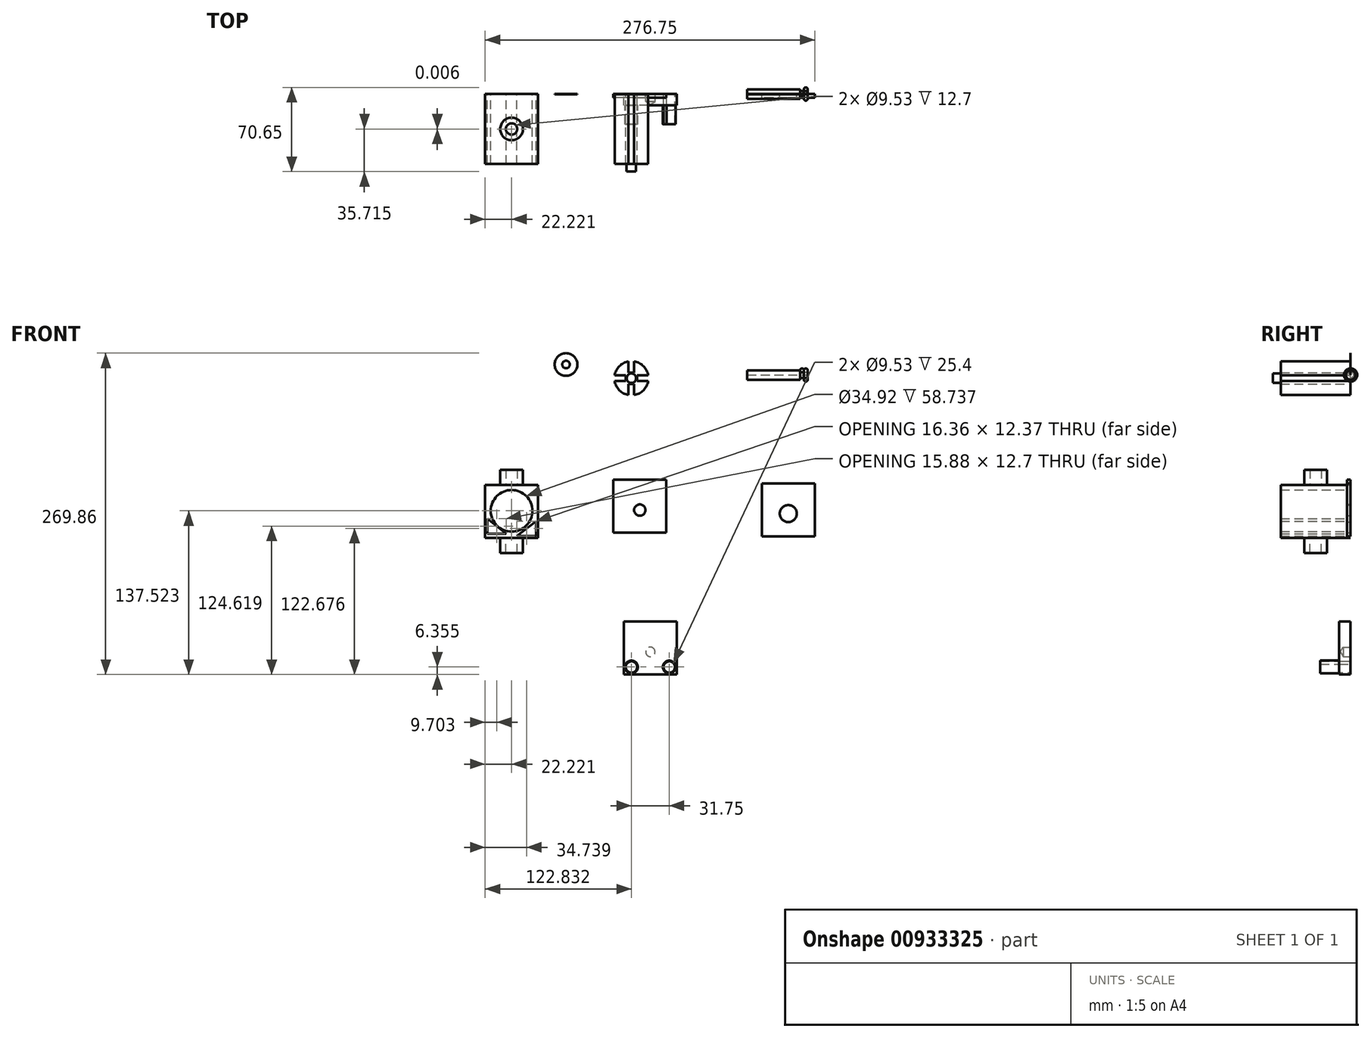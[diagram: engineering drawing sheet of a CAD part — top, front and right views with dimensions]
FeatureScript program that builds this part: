
annotation { "Feature Type Name" : "Feature", "Feature Type Description" : "" }
export const myFeature = defineFeature(function(context is Context, id is Id, definition is map)
    precondition{}
    {
        {
            var Q0;
            Q0=qCreatedBy(makeId("Front.planeOp"),FACE);
            var sketch = newSketch(context, id + "F0", { "sketchPlane" : qUnion([Q0])});
            skLineSegment(sketch, "E0.bottom", {"start": v(22.22, -22.22) * mm, "end": v(-22.23, -22.23) * mm});
            skLineSegment(sketch, "E0.top", {"start": v(22.22, 22.23) * mm, "end": v(-22.23, 22.22) * mm});
            skLineSegment(sketch, "E0.left", {"start": v(22.22, -22.22) * mm, "end": v(22.22, 22.23) * mm});
            skLineSegment(sketch, "E0.right", {"start": v(-22.23, -22.23) * mm, "end": v(-22.23, 22.23) * mm});
            skPoint(sketch, "E0.middle", {"position": v(0, 0) * mm});
            skCircle(sketch, "E1", {"center": v(0, 0) * mm, "radius": 17.46 * mm});
            skCircle(sketch, "E2", {"center": v(0, -3.18) * mm, "radius": 14.29 * mm, "construction": true});
            skCircle(sketch, "E3", {"center": v(0, -3.18) * mm, "radius": 7.14 * mm});
            skCircle(sketch, "E4", {"center": v(0, -3.18) * mm, "radius": 4.76 * mm});
            skLineSegment(sketch, "E5.bottom", {"start": v(-85.38, -26.4) * mm, "end": v(-129.83, -26.4) * mm});
            skLineSegment(sketch, "E5.top", {"start": v(-85.38, 18.05) * mm, "end": v(-129.83, 18.05) * mm});
            skLineSegment(sketch, "E5.left", {"start": v(-85.38, -26.4) * mm, "end": v(-85.38, 18.05) * mm});
            skLineSegment(sketch, "E5.right", {"start": v(-129.83, -26.4) * mm, "end": v(-129.83, 18.05) * mm});
            skCircle(sketch, "E6", {"center": v(-107.6, -3.79) * mm, "radius": 17.46 * mm});
            skCircle(sketch, "E7", {"center": v(-107.6, -6.96) * mm, "radius": 14.29 * mm, "construction": true});
            skCircle(sketch, "E8", {"center": v(-107.6, -6.96) * mm, "radius": 7.14 * mm});
            skCircle(sketch, "E9", {"center": v(-107.6, -6.96) * mm, "radius": 4.76 * mm});
            skLineSegment(sketch, "E10.bottom", {"start": v(146.92, -25.18) * mm, "end": v(102.47, -25.18) * mm});
            skLineSegment(sketch, "E10.top", {"start": v(146.92, 19.27) * mm, "end": v(102.47, 19.27) * mm});
            skLineSegment(sketch, "E10.left", {"start": v(146.92, -25.18) * mm, "end": v(146.92, 19.27) * mm});
            skLineSegment(sketch, "E10.right", {"start": v(102.47, -25.18) * mm, "end": v(102.47, 19.27) * mm});
            skCircle(sketch, "E11", {"center": v(124.7, -2.96) * mm, "radius": 17.46 * mm});
            skCircle(sketch, "E12", {"center": v(124.7, -6.13) * mm, "radius": 14.29 * mm, "construction": true});
            skCircle(sketch, "E13", {"center": v(124.7, -6.13) * mm, "radius": 7.14 * mm});
            skCircle(sketch, "E14", {"center": v(124.7, -6.13) * mm, "radius": 4.76 * mm});
            skLineSegment(sketch, "E15.bottom", {"start": v(31.1, -141.3) * mm, "end": v(-13.35, -141.3) * mm});
            skLineSegment(sketch, "E15.top", {"start": v(31.1, -96.86) * mm, "end": v(-13.35, -96.86) * mm});
            skLineSegment(sketch, "E15.left", {"start": v(31.1, -141.3) * mm, "end": v(31.1, -96.86) * mm});
            skLineSegment(sketch, "E15.right", {"start": v(-13.35, -141.3) * mm, "end": v(-13.35, -96.86) * mm});
            skCircle(sketch, "E16", {"center": v(8.88, -119.08) * mm, "radius": 17.46 * mm});
            skCircle(sketch, "E17", {"center": v(8.88, -122.26) * mm, "radius": 14.29 * mm, "construction": true});
            skCircle(sketch, "E18", {"center": v(8.88, -122.26) * mm, "radius": 7.14 * mm});
            skCircle(sketch, "E19", {"center": v(8.88, -122.26) * mm, "radius": 4.76 * mm});
            skCircle(sketch, "E20", {"center": v(8.88, -122.26) * mm, "radius": 3.97 * mm});
            skLineSegment(sketch, "E21", {"start": v(-86.91, -24.82) * mm, "end": v(-103.27, -24.82) * mm});
            skLineSegment(sketch, "E22", {"start": v(-103.27, -24.82) * mm, "end": v(-87.15, -12.45) * mm});
            skLineSegment(sketch, "E23", {"start": v(-87.15, -12.45) * mm, "end": v(-86.91, -24.82) * mm});
            skLineSegment(sketch, "E24", {"start": v(-112.19, -23.04) * mm, "end": v(-128.06, -23.04) * mm});
            skLineSegment(sketch, "E25", {"start": v(-128.06, -23.04) * mm, "end": v(-128.06, -10.34) * mm});
            skLineSegment(sketch, "E26", {"start": v(-128.06, -10.34) * mm, "end": v(-112.19, -23.04) * mm});
            skCircle(sketch, "E27", {"center": v(24.75, -134.96) * mm, "radius": 5.4 * mm});
            skCircle(sketch, "E28", {"center": v(-7, -134.96) * mm, "radius": 5.4 * mm});
            skCircle(sketch, "E29", {"center": v(24.75, -134.96) * mm, "radius": 4.76 * mm});
            skCircle(sketch, "E30", {"center": v(-7, -134.96) * mm, "radius": 4.76 * mm});
            skSolve(sketch);
        }
        {
            var Q0;
            Q0=makeQuery(id+"F0.imprint","IMPRINT",FACE,{"disambiguationData":[TD([[makeQuery(id+"F0.imprint","IMPRINT",EDGE,{"derivedFrom":sQuery(id+"F0.wireOp",EDGE,"E3")}),1.0]])]});
            var Q1;
            Q1=makeQuery(id+"F0.imprint","IMPRINT",FACE,{"disambiguationData":[TD([[makeQuery(id+"F0.imprint","IMPRINT",EDGE,{"derivedFrom":sQuery(id+"F0.wireOp",EDGE,"E0.bottom")}),-1.0]])]});
            var Q2;
            Q2=makeQuery(id+"F0.imprint","IMPRINT",FACE,{"disambiguationData":[TD([[makeQuery(id+"F0.imprint","IMPRINT",EDGE,{"derivedFrom":sQuery(id+"F0.wireOp",EDGE,"E1")}),1.0]])]});
            extrude(context, id + "F1", {"entities" : qUnion([Q0, Q1, Q2]), "depth" : 3.17 * mm, "offsetDistance" : 25.4 * mm});
        }
        {
            var Q0;
            Q0=makeQuery(id+"F0.imprint","IMPRINT",FACE,{"disambiguationData":[TD([[makeQuery(id+"F0.imprint","IMPRINT",EDGE,{"derivedFrom":sQuery(id+"F0.wireOp",EDGE,"E11")}),1.0]])]});
            var Q1;
            Q1=makeQuery(id+"F0.imprint","IMPRINT",FACE,{"disambiguationData":[TD([[makeQuery(id+"F0.imprint","IMPRINT",EDGE,{"derivedFrom":sQuery(id+"F0.wireOp",EDGE,"E10.bottom")}),-1.0]])]});
            extrude(context, id + "F2", {"entities" : qUnion([Q0, Q1]), "depth" : 3.17 * mm, "offsetDistance" : 25.4 * mm});
        }
        {
            var Q0;
            Q0=makeQuery(id+"F0.imprint","IMPRINT",FACE,{"disambiguationData":[TD([[makeQuery(id+"F0.imprint","IMPRINT",EDGE,{"derivedFrom":sQuery(id+"F0.wireOp",EDGE,"E5.bottom")}),-1.0]])]});
            extrude(context, id + "F3", {"entities" : qUnion([Q0]), "depth" : 58.74 * mm, "offsetDistance" : 25.4 * mm});
        }
        {
            var Q0;
            Q0=makeQuery(id+"F0.imprint","IMPRINT",FACE,{"disambiguationData":[TD([[makeQuery(id+"F0.imprint","IMPRINT",EDGE,{"derivedFrom":sQuery(id+"F0.wireOp",EDGE,"E18")}),1.0]])]});
            var Q1;
            Q1=makeQuery(id+"F0.imprint","IMPRINT",FACE,{"disambiguationData":[TD([[makeQuery(id+"F0.imprint","IMPRINT",EDGE,{"derivedFrom":sQuery(id+"F0.wireOp",EDGE,"E19")}),1.0]])]});
            var Q2;
            Q2=makeQuery(id+"F0.imprint","IMPRINT",FACE,{"disambiguationData":[TD([[makeQuery(id+"F0.imprint","IMPRINT",EDGE,{"derivedFrom":sQuery(id+"F0.wireOp",EDGE,"E20")}),1.0]])]});
            var Q3;
            Q3=makeQuery(id+"F0.imprint","IMPRINT",FACE,{"disambiguationData":[TD([[makeQuery(id+"F0.imprint","IMPRINT",EDGE,{"derivedFrom":sQuery(id+"F0.wireOp",EDGE,"E16")}),1.0]])]});
            var Q4;
            Q4=makeQuery(id+"F0.imprint","IMPRINT",FACE,{"disambiguationData":[TD([[makeQuery(id+"F0.imprint","IMPRINT",EDGE,{"derivedFrom":sQuery(id+"F0.wireOp",EDGE,"E15.bottom")}),-1.0]])]});
            extrude(context, id + "F4", {"entities" : qUnion([Q0, Q1, Q2, Q3, Q4]), "depth" : 9.52 * mm, "offsetDistance" : 25.4 * mm});
        }
        {
            var Q0;
            Q0=sQuery(id+"F0.wireOp",VERTEX,"E19.center");
            var Q1;
            Q1=makeQuery(id+"F4.opExtrude","SWEPT_BODY",BODY,{"disambiguationData":[OSD([sQuery(id+"F0.wireOp",EDGE,"E15.bottom"),sQuery(id+"F0.wireOp",EDGE,"E15.top"),sQuery(id+"F0.wireOp",EDGE,"E15.left"),sQuery(id+"F0.wireOp",EDGE,"E15.right")])]});
            hole(context, id + "F5", {"style" : HoleStyle.SIMPLE, "endStyle" : HoleEndStyle.BLIND, "oppositeDirection" : true, "holeDiameter" : 7.94 * mm, "majorDiameter" : 6.35 * mm, "holeDepth" : 6.35 * mm, "isTappedThrough" : true, "tappedDepth" : 12.7 * mm, "tapClearance" : 3, "locations" : qUnion([Q0]), "scope" : qUnion([Q1])});
        }
        {
            var Q0;
            Q0=qCreatedBy(makeId("Front.planeOp"),FACE);
            var sketch = newSketch(context, id + "F6", { "sketchPlane" : qUnion([Q0])});
            skArc(sketch, "E31", {"start": v(-4.66, 93.43) * mm, "mid": v(3.06, 97.41) * mm, "end": v(7.05, 105.14) * mm});
            skCircle(sketch, "E32", {"center": v(-7.04, 107.52) * mm, "radius": 3.97 * mm});
            skLineSegment(sketch, "E33.left", {"start": v(-4.66, 93.43) * mm, "end": v(-4.66, 102.75) * mm});
            skLineSegment(sketch, "E33.right", {"start": v(-9.42, 93.43) * mm, "end": v(-9.42, 102.75) * mm});
            skLineSegment(sketch, "E34.bottom", {"start": v(7.05, 105.14) * mm, "end": v(-2.28, 105.14) * mm});
            skLineSegment(sketch, "E34.top", {"start": v(7.05, 109.9) * mm, "end": v(-2.28, 109.9) * mm});
            skLineSegment(sketch, "E35", {"start": v(-9.42, 112.28) * mm, "end": v(-4.66, 112.28) * mm});
            skLineSegment(sketch, "E36.bottom", {"start": v(-4.66, 102.75) * mm, "end": v(-9.42, 102.75) * mm});
            skLineSegment(sketch, "E36.top", {"start": v(-4.66, 112.28) * mm, "end": v(-9.42, 112.28) * mm});
            skLineSegment(sketch, "E36.left", {"start": v(-2.28, 105.14) * mm, "end": v(-2.28, 109.9) * mm});
            skLineSegment(sketch, "E36.right", {"start": v(-11.8, 105.14) * mm, "end": v(-11.8, 109.9) * mm});
            skArc(sketch, "E37.trimOffspring", {"start": v(7.05, 109.9) * mm, "mid": v(3.06, 117.62) * mm, "end": v(-4.66, 121.6) * mm});
            skLineSegment(sketch, "E38.trimOffspring", {"start": v(-4.66, 112.28) * mm, "end": v(-4.66, 121.6) * mm});
            skLineSegment(sketch, "E39.trimOffspring", {"start": v(-11.8, 105.14) * mm, "end": v(-21.13, 105.14) * mm});
            skLineSegment(sketch, "E40.trimOffspring", {"start": v(-9.42, 112.28) * mm, "end": v(-9.42, 121.6) * mm});
            skArc(sketch, "E41.trimOffspring", {"start": v(-9.42, 121.6) * mm, "mid": v(-17.14, 117.62) * mm, "end": v(-21.13, 109.9) * mm});
            skLineSegment(sketch, "E42.trimOffspring", {"start": v(-11.8, 109.9) * mm, "end": v(-21.13, 109.9) * mm});
            skArc(sketch, "E43.trimOffspring", {"start": v(-21.13, 105.14) * mm, "mid": v(-17.14, 97.41) * mm, "end": v(-9.42, 93.43) * mm});
            skLineSegment(sketch, "E44", {"start": v(90.13, 110.2) * mm, "end": v(140.93, 110.2) * mm});
            skLineSegment(sketch, "E45", {"start": v(140.93, 110.2) * mm, "end": v(140.93, 114.17) * mm});
            skLineSegment(sketch, "E46", {"start": v(90.13, 114.17) * mm, "end": v(90.13, 110.2) * mm});
            skCircle(sketch, "E47", {"center": v(139.34, 114.17) * mm, "radius": 1.59 * mm});
            skCircle(sketch, "E48", {"center": v(136.17, 114.17) * mm, "radius": 1.59 * mm});
            skLineSegment(sketch, "E49.trimOffspring", {"start": v(134.58, 114.17) * mm, "end": v(90.13, 114.17) * mm});
            skCircle(sketch, "E50", {"center": v(-61.91, 119.03) * mm, "radius": 9.53 * mm});
            skCircle(sketch, "E51", {"center": v(-61.91, 119.03) * mm, "radius": 3.18 * mm});
            skSolve(sketch);
        }
        {
            var Q0;
            Q0=makeQuery(id+"F6.imprint","IMPRINT",FACE,{"disambiguationData":[TD([[makeQuery(id+"F6.imprint","IMPRINT",EDGE,{"derivedFrom":sQuery(id+"F6.wireOp",EDGE,"E31")}),1.0]])]});
            var Q1;
            Q1=makeQuery(id+"F6.imprint","IMPRINT",FACE,{"disambiguationData":[TD([[makeQuery(id+"F6.imprint","IMPRINT",EDGE,{"derivedFrom":sQuery(id+"F6.wireOp",EDGE,"E32")}),1.0]])]});
            extrude(context, id + "F7", {"entities" : qUnion([Q0, Q1]), "depth" : 58.74 * mm, "offsetDistance" : 25.4 * mm});
        }
        {
            var Q0;
            Q0=makeQuery(id+"F6.imprint","IMPRINT",FACE,{"disambiguationData":[TD([[makeQuery(id+"F6.imprint","IMPRINT",EDGE,{"derivedFrom":sQuery(id+"F6.wireOp",EDGE,"E32")}),1.0]])]});
            extrude(context, id + "F8", {"entities" : qUnion([Q0]), "operationType" : NewBodyOperationType.ADD, "depth" : 65.1 * mm, "offsetDistance" : 25.4 * mm});
        }
        {
            var Q0;
            Q0=makeQuery(id+"F6.imprint","IMPRINT",FACE,{"disambiguationData":[TD([[makeQuery(id+"F6.imprint","IMPRINT",EDGE,{"derivedFrom":sQuery(id+"F6.wireOp",EDGE,"E44")}),1.0]])]});
            var Q1;
            Q1=sQuery(id+"F6.wireOp",EDGE,"E44");
            revolve(context, id + "F9", {"surfaceOperationType" : NewSurfaceOperationType.NEW, "entities" : qUnion([Q0]), "axis" : qUnion([Q1]), "revolveType" : RevolveType.FULL});
        }
        {
            var Q0;
            {var subQ0=sQuery(id+"F6.wireOp",EDGE,"E47");var subQ1=makeQuery(id+"F6.imprint","INTERSECT",VERTEX,{"derivedFrom":[sQuery(id+"F6.wireOp",EDGE,"E45"),subQ0]});Q0=makeQuery(id+"F6.imprint","IMPRINT",FACE,{"disambiguationData":[TD([[makeQuery(id+"F6.imprint","IMPRINT",EDGE,{"disambiguationData":[TD([[subQ1,-1.0]])],"derivedFrom":subQ0}),1.0]])]});}
            var Q1;
            Q1=sQuery(id+"F6.wireOp",EDGE,"E44");
            revolve(context, id + "F10", {"surfaceOperationType" : NewSurfaceOperationType.NEW, "entities" : qUnion([Q0]), "axis" : qUnion([Q1]), "revolveType" : RevolveType.FULL});
        }
        {
            var Q0;
            Q0 = qSketchRegion(id + "F6", true);
            extrude(context, id + "F11", {"entities" : qUnion([Q0]), "depth" : 0.16 * mm, "offsetDistance" : 25.4 * mm});
        }
        {
            var Q0;
            Q0=makeQuery(id+"F0.imprint","IMPRINT",FACE,{"disambiguationData":[TD([[makeQuery(id+"F0.imprint","IMPRINT",EDGE,{"derivedFrom":sQuery(id+"F0.wireOp",EDGE,"E29")}),-1.0]])]});
            var Q1;
            Q1=makeQuery(id+"F0.imprint","IMPRINT",FACE,{"disambiguationData":[TD([[makeQuery(id+"F0.imprint","IMPRINT",EDGE,{"derivedFrom":sQuery(id+"F0.wireOp",EDGE,"E30")}),-1.0]])]});
            extrude(context, id + "F12", {"entities" : qUnion([Q0, Q1]), "operationType" : NewBodyOperationType.ADD, "depth" : 25.4 * mm, "offsetDistance" : 25.4 * mm});
        }
        {
            var Q0;
            Q0=makeQuery(id+"F3.opExtrude","SWEPT_FACE",FACE,{"disambiguationData":[OSD([sQuery(id+"F0.wireOp",EDGE,"E5.top")])]});
            var sketch = newSketch(context, id + "F13", { "sketchPlane" : qUnion([Q0])});
            skLineSegment(sketch, "E52.bottom", {"start": v(-129.83, 0) * mm, "end": v(-85.38, 0) * mm});
            skLineSegment(sketch, "E52.top", {"start": v(-129.83, -58.74) * mm, "end": v(-85.38, -58.74) * mm});
            skLineSegment(sketch, "E52.left", {"start": v(-129.83, 0) * mm, "end": v(-129.83, -58.74) * mm});
            skLineSegment(sketch, "E52.right", {"start": v(-85.38, 0) * mm, "end": v(-85.38, -58.74) * mm});
            skCircle(sketch, "E53", {"center": v(-107.6, -29.37) * mm, "radius": 9.53 * mm});
            skPoint(sketch, "E53.centerSnap0", {"position": v(-107.6, -58.74) * mm});
            skPoint(sketch, "E53.centerSnap1", {"position": v(-129.83, -29.37) * mm});
            skCircle(sketch, "E54", {"center": v(-107.6, -29.37) * mm, "radius": 4.76 * mm});
            skSolve(sketch);
        }
        {
            var Q0;
            Q0=makeQuery(id+"F13.imprint","IMPRINT",FACE,{"disambiguationData":[TD([[makeQuery(id+"F13.imprint","IMPRINT",EDGE,{"derivedFrom":sQuery(id+"F13.wireOp",EDGE,"E53")}),1.0]])]});
            extrude(context, id + "F14", {"entities" : qUnion([Q0]), "operationType" : NewBodyOperationType.ADD, "depth" : 12.7 * mm, "offsetDistance" : 25.4 * mm});
        }
        {
            var Q0;
            Q0=makeQuery(id+"F3.opExtrude","SWEPT_FACE",FACE,{"disambiguationData":[OSD([sQuery(id+"F0.wireOp",EDGE,"E5.bottom")])]});
            var sketch = newSketch(context, id + "F15", { "sketchPlane" : qUnion([Q0])});
            skCircle(sketch, "E55", {"center": v(-107.6, 29.38) * mm, "radius": 4.76 * mm});
            skCircle(sketch, "E56", {"center": v(-107.6, 29.38) * mm, "radius": 9.53 * mm});
            skSolve(sketch);
        }
        {
            var Q0;
            Q0=makeQuery(id+"F15.imprint","IMPRINT",FACE,{"disambiguationData":[TD([[makeQuery(id+"F15.imprint","IMPRINT",EDGE,{"derivedFrom":sQuery(id+"F15.wireOp",EDGE,"E55")}),-1.0]])]});
            extrude(context, id + "F16", {"entities" : qUnion([Q0]), "operationType" : NewBodyOperationType.ADD, "depth" : 12.7 * mm, "offsetDistance" : 25.4 * mm});
        }
    });
